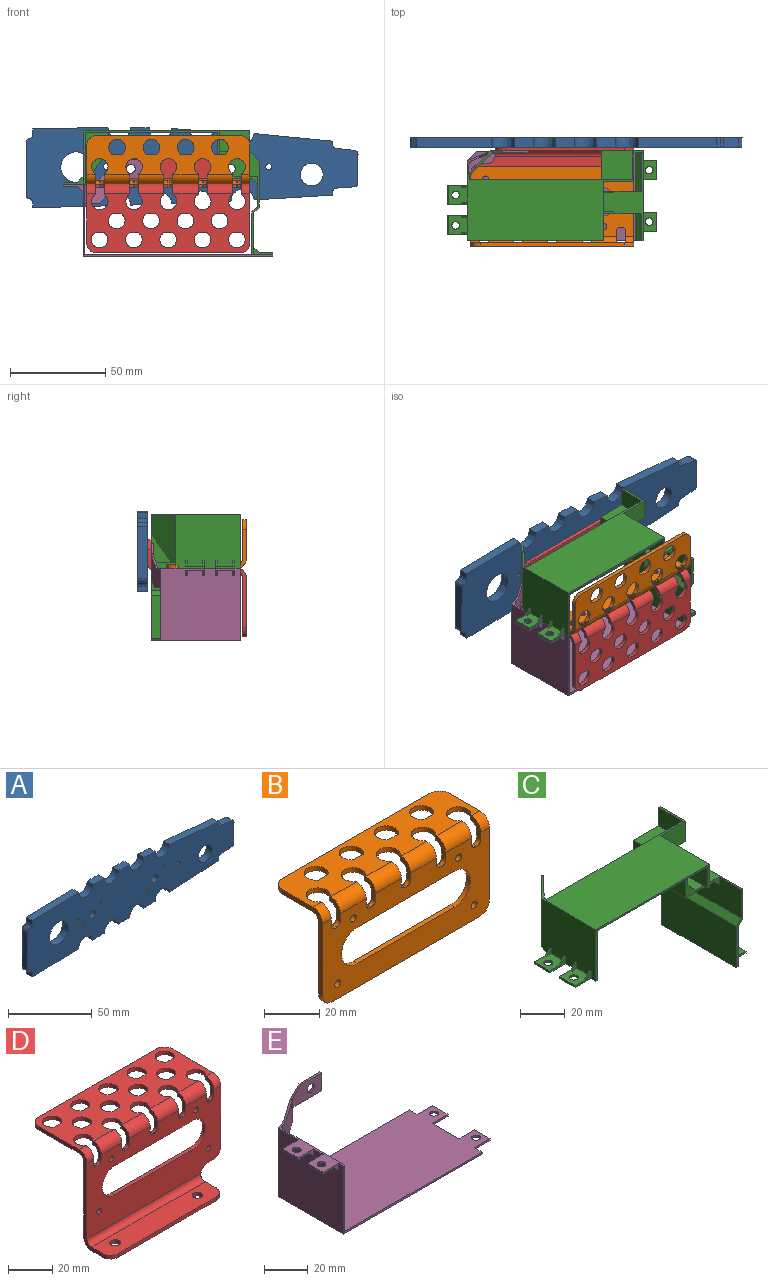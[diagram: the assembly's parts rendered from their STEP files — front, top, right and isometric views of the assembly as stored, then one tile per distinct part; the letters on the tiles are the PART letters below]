
ASSEMBLY  parts=5 mates=7
PART A: 65 faces, bbox 174.9x5.8x42.9 mm
  f0: plane 5x0.18mm, normal (1,0,-0.01), area 0.9mm2, adj f5,f6,f61,f62
  f1: plane 5x0.04mm, normal (1,0,0), area 0.2mm2, adj f7,f8,f61,f62
  f2: plane 5x0.19mm, normal (1,0,0.01), area 0.9mm2, adj f16,f17,f61,f62
  f3: plane 5x0.23mm, normal (1,0,0.02), area 1.1mm2, adj f18,f19,f61,f62
  f4: extruded ~5x0.27mm, area 1.3mm2, adj f20,f21,f61,f62
  f5: extruded ~12.02x6mm, area 93.3mm2, adj f0,f42,f61,f62
  f6: cylinder r=940.53mm len=9.52mm, axis (0,-1,0), area 47.6mm2, adj f0,f7,f61,f62
  f7: extruded ~12.02x6mm, area 94mm2, adj f1,f6,f61,f62
  f8: extruded ~39.35x5mm, area 196.8mm2, adj f1,f9,f61,f62
  f9: plane 5x3.1mm, normal (-1,0,0), area 15.5mm2, adj f8,f10,f61,f62
  f10: extruded ~5x1.99mm, area 14.8mm2, adj f9,f11,f61,f62
  f11: cylinder r=2mm len=5mm, axis (0,-1,0), area 14.7mm2, adj f10,f12,f61,f62
  f12: plane 27.58x5mm, normal (-1,0,0), area 137.9mm2, adj f11,f13,f61,f62
  f13: cylinder r=2mm len=5mm, axis (0,1,0), area 14.7mm2, adj f12,f14,f61,f62
  f14: cylinder r=2mm len=5mm, axis (0,-1,0), area 14.8mm2, adj f13,f15,f61,f62
  f15: plane 5x2.6mm, normal (-1,0,0), area 13mm2, adj f14,f16,f61,f62
  f16: cylinder r=2986.1mm len=39.35mm, axis (0,-1,0), area 196.8mm2, adj f2,f15,f61,f62
  f17: extruded ~12.02x6mm, area 93.4mm2, adj f2,f18,f61,f62
  f18: cylinder r=3206.8mm len=9.52mm, axis (0,-1,0), area 47.7mm2, adj f3,f17,f61,f62
  f19: extruded ~12.02x6mm, area 93.1mm2, adj f3,f20,f61,f62
  f20: cylinder r=3333.11mm len=9.53mm, axis (0,-1,0), area 47.7mm2, adj f4,f19,f61,f62
  f21: extruded ~12.01x6mm, area 92.9mm2, adj f4,f22,f61,f62
  f22: cylinder r=3235.66mm len=9.53mm, axis (0,-1,0), area 47.7mm2, adj f21,f23,f61,f62
  f23: cylinder r=5.99mm len=5mm, axis (0,-1,0), area 1.5mm2, adj f22,f24,f61,f62
  f24: extruded ~12.01x6mm, area 92.7mm2, adj f23,f25,f61,f62
  f25: cylinder r=2917.73mm len=41.28mm, axis (0,-1,0), area 206.8mm2, adj f24,f26,f61,f62
  f26: plane 5x1.64mm, normal (1,0,0), area 8.2mm2, adj f25,f27,f61,f62
  f27: cylinder r=2mm len=5mm, axis (0,-1,0), area 15mm2, adj f26,f28,f61,f62
  f28: cylinder r=2837.04mm len=9.53mm, axis (0,-1,0), area 47.8mm2, adj f27,f29,f61,f62
  f29: cylinder r=2mm len=5mm, axis (0,-1,0), area 15mm2, adj f28,f30,f61,f62
  f30: plane 15.11x5mm, normal (1,0,0), area 75.5mm2, adj f29,f31,f61,f62
  f31: cylinder r=2mm len=5mm, axis (0,1,0), area 14.5mm2, adj f30,f32,f61,f62
  f32: extruded ~7.89x5mm, area 39.7mm2, adj f31,f33,f61,f62
  f33: plane 5x1.83mm, normal (0.11,0,0.99), area 9.2mm2, adj f32,f34,f61,f62
  f34: cylinder r=2mm len=5mm, axis (0,1,0), area 14.6mm2, adj f33,f35,f61,f62
  f35: plane 5x1.73mm, normal (1,0,0), area 8.7mm2, adj f34,f36,f61,f62
  f36: extruded ~41.29x5mm, area 207.4mm2, adj f35,f37,f61,f62
  f37: extruded ~12x6mm, area 92mm2, adj f36,f38,f61,f62
  f38: cylinder r=5.99mm len=5mm, axis (0,1,0), area 2.1mm2, adj f37,f39,f61,f62
  f39: cylinder r=1085.79mm len=9.54mm, axis (0,-1,0), area 47.8mm2, adj f38,f40,f61,f62
  f40: extruded ~12.01x6mm, area 92.6mm2, adj f39,f41,f61,f62
  f41: cylinder r=5.99mm len=5mm, axis (0,1,0), area 1.5mm2, adj f40,f42,f61,f62
  f42: cylinder r=1001.33mm len=9.53mm, axis (0,-1,0), area 47.7mm2, adj f5,f41,f61,f62
  f43: cylinder r=1mm len=5mm, axis (0,-1,0), area 15.7mm2, adj f44,f61,f62
  f44: cylinder r=1mm len=5mm, axis (0,-1,0), area 15.7mm2, adj f43,f61,f62
  f45: cylinder r=1mm len=5mm, axis (0,-1,0), area 15.7mm2, adj f46,f61,f62
  f46: cylinder r=1mm len=5mm, axis (0,-1,0), area 15.7mm2, adj f45,f61,f62
  f47: cylinder r=1mm len=5mm, axis (0,-1,0), area 15.7mm2, adj f48,f61,f62
  f48: cylinder r=1mm len=5mm, axis (0,-1,0), area 15.7mm2, adj f47,f61,f62
  f49: cylinder r=1mm len=5mm, axis (0,-1,0), area 15.7mm2, adj f50,f61,f62
  f50: cylinder r=1mm len=5mm, axis (0,-1,0), area 15.7mm2, adj f49,f61,f62
  f51: cylinder r=2.75mm len=5.16mm, axis (0,1,0), area 43.2mm2, adj f52,f61,f62
  f52: cylinder r=2.75mm len=5.16mm, axis (0,1,0), area 43.2mm2, adj f51,f61,f62
  f53: cylinder r=2.75mm len=5.16mm, axis (0,1,0), area 43.2mm2, adj f54,f61,f62
  f54: cylinder r=2.75mm len=5.16mm, axis (0,1,0), area 43.2mm2, adj f53,f61,f62
  f55: cylinder r=1.55mm len=5mm, axis (0,1,0), area 24.3mm2, adj f56,f61,f62
  f56: cylinder r=1.55mm len=5mm, axis (0,1,0), area 24.3mm2, adj f55,f61,f62
  f57: cylinder r=6mm len=11.27mm, axis (0,1,0), area 94.2mm2, adj f58,f61,f62
  f58: cylinder r=6mm len=11.27mm, axis (0,1,0), area 94.2mm2, adj f57,f61,f62
  f59: extruded ~16.06x8mm, area 125.9mm2, adj f60,f61,f62
  f60: extruded ~16.06x8mm, area 125.9mm2, adj f59,f61,f62
  f61: plane 174.9x42.87mm, normal (0,-1,0), area 5425.6mm2, adj f0,f1,f2,f3,f4,f5,f6,f7
  f62: plane 174.9x42.87mm, normal (0,1,0), area 5425.7mm2, adj f0,f1,f2,f3,f4,f5,f6,f7
  f63: cylinder r=1.55mm len=5mm, axis (0,1,0), area 24.3mm2, adj f61,f62,f64
  f64: cylinder r=1.55mm len=5mm, axis (0,1,0), area 24.3mm2, adj f61,f62,f63
PART B: 84 faces, bbox 85.5x25.5x42 mm
  f0: cylinder r=4.35mm len=8.7mm, axis (0,0,1), area 27.3mm2, adj f15,f16,f25,f27
  f1: cylinder r=4.35mm len=8.7mm, axis (0,0,1), area 27.3mm2, adj f17,f18,f25,f27
  f2: cylinder r=4.35mm len=8.7mm, axis (0,0,1), area 27.3mm2, adj f19,f20,f25,f27
  f3: cylinder r=4.35mm len=8.7mm, axis (0,0,1), area 27.3mm2, adj f21,f22,f25,f27
  f4: plane 75.54x2mm, normal (0,1,0), area 151.1mm2, adj f23,f24,f25,f27
  f5: cylinder r=4.35mm len=8.7mm, axis (0,0,1), area 27.3mm2, adj f14,f25,f26,f27
  f6: plane 4.73x2mm, normal (0,1,0), area 9.5mm2, adj f7,f25,f27
  f7: cylinder r=4.35mm len=8.7mm, axis (0,0,1), area 44.7mm2, adj f6,f25,f27
  f8: plane 4.73x2mm, normal (0,1,0), area 9.5mm2, adj f9,f25,f27
  f9: cylinder r=4.35mm len=8.7mm, axis (0,0,1), area 44.7mm2, adj f8,f25,f27
  f10: plane 4.73x2mm, normal (0,1,0), area 9.5mm2, adj f11,f25,f27
  f11: cylinder r=4.35mm len=8.7mm, axis (0,0,1), area 44.7mm2, adj f10,f25,f27
  f12: cylinder r=4.35mm len=8.7mm, axis (0,0,1), area 44.7mm2, adj f13,f25,f27
  f13: plane 4.73x2mm, normal (0,1,0), area 9.5mm2, adj f12,f25,f27
  f14: cylinder r=4.35mm len=3.65mm, axis (0,0,1), area 8.7mm2, adj f5,f25,f27,f34
  f15: cylinder r=4.35mm len=3.65mm, axis (0,0,1), area 8.7mm2, adj f0,f25,f27,f36
  f16: cylinder r=4.35mm len=3.65mm, axis (0,0,1), area 8.7mm2, adj f0,f25,f27,f40
  f17: cylinder r=4.35mm len=3.65mm, axis (0,0,1), area 8.7mm2, adj f1,f25,f27,f42
  f18: cylinder r=4.35mm len=3.65mm, axis (0,0,1), area 8.7mm2, adj f1,f25,f27,f46
  f19: cylinder r=4.35mm len=3.65mm, axis (0,0,1), area 8.7mm2, adj f2,f25,f27,f48
  f20: cylinder r=4.35mm len=3.65mm, axis (0,0,1), area 8.7mm2, adj f2,f25,f27,f52
  f21: cylinder r=4.35mm len=3.65mm, axis (0,0,1), area 8.7mm2, adj f3,f25,f27,f54
  f22: cylinder r=4.35mm len=3.65mm, axis (0,0,1), area 8.7mm2, adj f3,f25,f27,f58
  f23: cylinder r=5mm len=5mm, axis (0,0,1), area 15.7mm2, adj f4,f25,f27,f60
  f24: cylinder r=5mm len=5mm, axis (0,0,1), area 15.7mm2, adj f4,f25,f27,f64
  f25: plane 85.54x20.45mm, normal (0,0,-1), area 1214.1mm2, adj f0,f1,f2,f3,f4,f5,f6,f7
  f26: cylinder r=4.35mm len=3.65mm, axis (0,0,1), area 8.7mm2, adj f5,f25,f27,f66
  f27: plane 85.54x20.45mm, normal (0,0,1), area 1214.1mm2, adj f0,f1,f2,f3,f4,f5,f6,f7
  f28: cylinder r=5mm len=5mm, axis (1,0,0), area 34.6mm2, adj f27,f64,f66,f80
  f29: cylinder r=5mm len=5mm, axis (-1,0,0), area 34.6mm2, adj f27,f58,f60,f80
  f30: cylinder r=5mm len=13.27mm, axis (-1,0,0), area 104.2mm2, adj f27,f52,f54,f80
  f31: cylinder r=5mm len=13.27mm, axis (-1,0,0), area 104.2mm2, adj f27,f46,f48,f80
  f32: cylinder r=5mm len=13.27mm, axis (-1,0,0), area 104.2mm2, adj f27,f40,f42,f80
  f33: cylinder r=5mm len=13.27mm, axis (-1,0,0), area 104.2mm2, adj f27,f34,f36,f80
  f34: plane 8x5.41mm, normal (1,0,0), area 19.4mm2, adj f14,f25,f27,f33,f35,f69,f80,f82
  f35: cylinder r=3mm len=13.27mm, axis (1,0,0), area 62.5mm2, adj f25,f34,f36,f82
  f36: plane 8x5.41mm, normal (-1,0,0), area 19.4mm2, adj f15,f25,f27,f33,f35,f37,f80,f82
  f37: cylinder r=2mm len=2mm, axis (0,1,0), area 6.3mm2, adj f36,f38,f80,f82
  f38: plane 2x0.73mm, normal (0,0,1), area 1.5mm2, adj f37,f39,f80,f82
  f39: cylinder r=2mm len=2mm, axis (0,1,0), area 6.3mm2, adj f38,f40,f80,f82
  f40: plane 8x5.41mm, normal (1,0,0), area 19.4mm2, adj f16,f25,f27,f32,f39,f41,f80,f82
  f41: cylinder r=3mm len=13.27mm, axis (-1,0,0), area 62.5mm2, adj f25,f40,f42,f82
  f42: plane 8x5.41mm, normal (-1,0,0), area 19.4mm2, adj f17,f25,f27,f32,f41,f43,f80,f82
  f43: cylinder r=2mm len=2mm, axis (0,1,0), area 6.3mm2, adj f42,f44,f80,f82
  f44: plane 2x0.73mm, normal (0,0,1), area 1.5mm2, adj f43,f45,f80,f82
  f45: cylinder r=2mm len=2mm, axis (0,1,0), area 6.3mm2, adj f44,f46,f80,f82
  f46: plane 8x5.41mm, normal (1,0,0), area 19.4mm2, adj f18,f25,f27,f31,f45,f47,f80,f82
  f47: cylinder r=3mm len=13.27mm, axis (-1,0,0), area 62.5mm2, adj f25,f46,f48,f82
  f48: plane 8x5.41mm, normal (-1,0,0), area 19.4mm2, adj f19,f25,f27,f31,f47,f49,f80,f82
  f49: cylinder r=2mm len=2mm, axis (0,1,0), area 6.3mm2, adj f48,f50,f80,f82
  f50: plane 2x0.73mm, normal (0,0,1), area 1.5mm2, adj f49,f51,f80,f82
  f51: cylinder r=2mm len=2mm, axis (0,1,0), area 6.3mm2, adj f50,f52,f80,f82
  f52: plane 8x5.41mm, normal (1,0,0), area 19.4mm2, adj f20,f25,f27,f30,f51,f53,f80,f82
  f53: cylinder r=3mm len=13.27mm, axis (-1,0,0), area 62.5mm2, adj f25,f52,f54,f82
  f54: plane 8x5.41mm, normal (-1,0,0), area 19.4mm2, adj f21,f25,f27,f30,f53,f55,f80,f82
  f55: cylinder r=2mm len=2mm, axis (0,1,0), area 6.3mm2, adj f54,f56,f80,f82
  f56: plane 2x0.73mm, normal (0,0,1), area 1.5mm2, adj f55,f57,f80,f82
  f57: cylinder r=2mm len=2mm, axis (0,1,0), area 6.3mm2, adj f56,f58,f80,f82
  f58: plane 8x5.41mm, normal (1,0,0), area 19.4mm2, adj f22,f25,f27,f29,f57,f59,f80,f82
  f59: cylinder r=3mm len=4.4mm, axis (-1,0,0), area 20.7mm2, adj f25,f58,f60,f82
  f60: plane 37x20.45mm, normal (-1,0,0), area 107.5mm2, adj f23,f25,f27,f29,f59,f61,f80,f82
  f61: cylinder r=5mm len=5mm, axis (0,-1,0), area 15.7mm2, adj f60,f62,f80,f82
  f62: plane 75.54x2mm, normal (0,0,-1), area 151.1mm2, adj f61,f63,f80,f82
  f63: cylinder r=5mm len=5mm, axis (0,1,0), area 15.7mm2, adj f62,f64,f80,f82
  f64: plane 37x20.45mm, normal (1,0,0), area 107.5mm2, adj f24,f25,f27,f28,f63,f65,f80,f82
  f65: cylinder r=3mm len=4.4mm, axis (1,0,0), area 20.7mm2, adj f25,f64,f66,f82
  f66: plane 8x5.41mm, normal (-1,0,0), area 19.4mm2, adj f25,f26,f27,f28,f65,f67,f80,f82
  f67: cylinder r=2mm len=2mm, axis (0,1,0), area 6.3mm2, adj f66,f68,f80,f82
  f68: plane 2x0.73mm, normal (0,0,1), area 1.5mm2, adj f67,f69,f80,f82
  f69: cylinder r=2mm len=2mm, axis (0,1,0), area 6.3mm2, adj f34,f68,f80,f82
  f70: plane 50x2mm, normal (0,0,1), area 100mm2, adj f71,f73,f80,f82
  f71: cylinder r=8mm len=16mm, axis (0,1,0), area 50.3mm2, adj f70,f72,f80,f82
  f72: plane 50x2mm, normal (0,0,-1), area 100mm2, adj f71,f73,f80,f82
  f73: cylinder r=8mm len=16mm, axis (0,1,0), area 50.3mm2, adj f70,f72,f80,f82
  f74: cylinder r=1.5mm len=3mm, axis (0,1,0), area 9.4mm2, adj f75,f80,f82
  f75: cylinder r=1.5mm len=3mm, axis (0,1,0), area 9.4mm2, adj f74,f80,f82
  f76: cylinder r=1.5mm len=3mm, axis (0,1,0), area 9.4mm2, adj f77,f80,f82
  f77: cylinder r=1.5mm len=3mm, axis (0,1,0), area 9.4mm2, adj f76,f80,f82
  f78: cylinder r=1.5mm len=3mm, axis (0,1,0), area 9.4mm2, adj f79,f80,f82
  f79: cylinder r=1.5mm len=3mm, axis (0,1,0), area 9.4mm2, adj f78,f80,f82
  f80: plane 85.54x37mm, normal (0,-1,0), area 2015mm2, adj f28,f29,f30,f31,f32,f33,f34,f36
  f81: cylinder r=1.5mm len=3mm, axis (0,1,0), area 9.4mm2, adj f80,f82,f83
  f82: plane 85.54x37mm, normal (0,1,0), area 2015mm2, adj f34,f35,f36,f37,f38,f39,f40,f41
  f83: cylinder r=1.5mm len=3mm, axis (0,1,0), area 9.4mm2, adj f80,f81,f82
PART C: 83 faces, bbox 109.5x47x65 mm
  f0: plane 3x3mm, normal (-0.71,0,0.71), area 4.2mm2, adj f4,f72,f74,f78
  f1: plane 3x3mm, normal (-0.71,0,0.71), area 4.2mm2, adj f4,f73,f74,f79
  f2: plane 3x3mm, normal (-0.71,0,0.71), area 4.2mm2, adj f4,f68,f70,f76
  f3: plane 3x3mm, normal (-0.71,0,0.71), area 4.2mm2, adj f4,f69,f70,f77
  f4: plane 34x28mm, normal (-1,0,0), area 918.1mm2, adj f0,f1,f2,f3,f17,f18,f30,f66
  f5: plane 2.57x1.84mm, normal (0,0,-1), area 2.1mm2, adj f16,f30,f31,f33,f67
  f6: plane 47x15.59mm, normal (-1,0,0), area 710.5mm2, adj f10,f11,f12,f13,f23,f24,f39,f40
  f7: plane 3x3mm, normal (0.71,0,0.71), area 4.2mm2, adj f9,f53,f54,f63
  f8: plane 3x3mm, normal (0.71,0,0.71), area 4.2mm2, adj f9,f48,f50,f59
  f9: plane 47x22mm, normal (1,0,0), area 1002mm2, adj f7,f8,f24,f39,f44,f47,f48,f49
  f10: plane 33x21mm, normal (0,0,-1), area 284mm2, adj f6,f11,f12,f14,f15,f23,f24,f40
  f11: plane 21x15.5mm, normal (0,-1,0), area 52.1mm2, adj f6,f10,f13,f14,f15,f29,f35,f40
  f12: plane 20x9.5mm, normal (0,1,0), area 39.6mm2, adj f6,f10,f13,f14,f37,f42
  f13: plane 46x21mm, normal (0,0,1), area 275mm2, adj f6,f11,f12,f14,f23,f34,f35,f36
  f14: plane 46x25mm, normal (1,0,0), area 787mm2, adj f10,f11,f12,f13,f18,f23,f25,f28
  f15: plane 47x24mm, normal (-1,0,0), area 818mm2, adj f10,f11,f19,f20,f24,f27,f29,f82
  f16: plane 35x28mm, normal (1,0,0), area 908.5mm2, adj f5,f17,f18,f19,f20,f31,f66,f67
  f17: plane 27.01x1.01mm, normal (0,-1,0), area 27mm2, adj f4,f16,f66,f82
  f18: plane 87.5x47mm, normal (0,0,1), area 2338.8mm2, adj f4,f14,f16,f19,f22,f24,f26,f28
  f19: plane 85.5x10mm, normal (0,1,0), area 229.5mm2, adj f15,f16,f18,f20,f26,f27
  f20: plane 69.5x32mm, normal (0,0,-1), area 2224.2mm2, adj f15,f16,f19,f82
  f21: cylinder r=2.35mm len=4.7mm, axis (0,1,0), area 14.8mm2, adj f23,f24
  f22: plane 16x11mm, normal (1,0,0), area 176mm2, adj f18,f24,f25,f28,f64
  f23: plane 21x17mm, normal (0,-1,0), area 267.7mm2, adj f6,f10,f13,f14,f21,f25,f34,f64
  f24: plane 65x22mm, normal (0,1,0), area 350.9mm2, adj f6,f9,f10,f15,f18,f21,f22,f26
  f25: plane 16x15mm, normal (0,0,-1), area 240mm2, adj f14,f22,f23,f28
  f26: plane 15x10mm, normal (-1,0,0), area 150mm2, adj f18,f19,f24,f27
  f27: plane 16x15mm, normal (0,0,1), area 240mm2, adj f15,f19,f24,f26
  f28: plane 16x11mm, normal (0,-1,0), area 176mm2, adj f14,f18,f22,f25
  f29: plane 14x1mm, normal (0,0,-1), area 14mm2, adj f11,f14,f15,f82
  f30: plane 26x13mm, normal (-0.72,0.69,0), area 338.2mm2, adj f4,f5,f18,f32,f33,f67
  f31: plane 25x12.71mm, normal (0.72,-0.69,0), area 327.5mm2, adj f5,f16,f18,f32,f33
  f32: plane 10x0.72mm, normal (0.69,0.72,0), area 10mm2, adj f18,f30,f31,f33
  f33: plane 15x11.53mm, normal (0.49,0.51,-0.71), area 21.2mm2, adj f5,f30,f31,f32
  f34: plane 47x24mm, normal (1,0,0), area 760mm2, adj f13,f23,f24,f39,f44,f64
  f35: plane 5.5x5.5mm, normal (0.71,0,0.71), area 7.8mm2, adj f11,f13,f14,f36
  f36: plane 5.5x5.5mm, normal (0,1,0), area 15.1mm2, adj f13,f14,f35
  f37: plane 5.5x5.5mm, normal (0.71,0,0.71), area 7.8mm2, adj f12,f13,f14,f38
  f38: plane 5.5x5.5mm, normal (0,-1,0), area 15.1mm2, adj f13,f14,f37
  f39: plane 41x4mm, normal (0,-1,0), area 42.2mm2, adj f6,f9,f13,f34,f44,f45,f46,f47
  f40: plane 3x3mm, normal (-0.71,0,-0.71), area 4.2mm2, adj f6,f10,f11,f41
  f41: plane 3x3mm, normal (0,1,0), area 4.5mm2, adj f6,f10,f40
  f42: plane 3x3mm, normal (-0.71,0,-0.71), area 4.2mm2, adj f6,f10,f12,f43
  f43: plane 3x3mm, normal (0,-1,0), area 4.5mm2, adj f6,f10,f42
  f44: plane 47x3mm, normal (0.71,0,-0.71), area 199.4mm2, adj f9,f24,f34,f39
  f45: plane 47x3mm, normal (-0.71,0,0.71), area 199.4mm2, adj f6,f24,f39,f46
  f46: plane 47x22.41mm, normal (-1,0,0), area 1053.5mm2, adj f24,f39,f45,f47
  f47: plane 47x11mm, normal (0,0,-1), area 221.9mm2, adj f9,f24,f39,f46,f48,f49,f51,f52
  f48: plane 10x4mm, normal (0,-1,0), area 14.5mm2, adj f8,f9,f47,f50,f51
  f49: plane 10x4mm, normal (0,1,0), area 14.5mm2, adj f9,f47,f50,f51,f58
  f50: plane 10x10mm, normal (0,0,1), area 81.4mm2, adj f8,f9,f48,f49,f51,f57,f58,f59
  f51: plane 10x1mm, normal (1,0,0), area 10mm2, adj f47,f48,f49,f50
  f52: plane 10x4mm, normal (0,1,0), area 14.5mm2, adj f9,f47,f53,f55,f61
  f53: plane 10x10mm, normal (0,0,1), area 81.4mm2, adj f7,f9,f52,f54,f55,f56,f61,f62
  f54: plane 10x4mm, normal (0,-1,0), area 14.5mm2, adj f7,f9,f47,f53,f55
  f55: plane 10x1mm, normal (1,0,0), area 10mm2, adj f47,f52,f53,f54
  f56: cylinder r=2mm len=4mm, axis (0,0,1), area 12.6mm2, adj f47,f53
  f57: cylinder r=2mm len=4mm, axis (0,0,1), area 12.6mm2, adj f47,f50
  f58: plane 3x3mm, normal (0.71,0,0.71), area 4.2mm2, adj f9,f49,f50,f60
  f59: plane 3x3mm, normal (0,1,0), area 4.5mm2, adj f8,f9,f50
  f60: plane 3x3mm, normal (0,-1,0), area 4.5mm2, adj f9,f50,f58
  f61: plane 3x3mm, normal (0.71,0,0.71), area 4.2mm2, adj f9,f52,f53,f62
  f62: plane 3x3mm, normal (0,-1,0), area 4.5mm2, adj f9,f53,f61
  f63: plane 3x3mm, normal (0,1,0), area 4.5mm2, adj f7,f9,f53
  f64: plane 5x5mm, normal (0.71,0,0.71), area 7.1mm2, adj f22,f23,f24,f34
  f65: plane 3x3mm, normal (-0.71,0,-0.71), area 4.2mm2, adj f6,f10,f23,f24
  f66: plane 32x11mm, normal (0,0,-1), area 206.9mm2, adj f4,f16,f17,f67,f68,f69,f71,f72
  f67: plane 3x3mm, normal (0,0.71,-0.71), area 3.6mm2, adj f4,f5,f16,f30,f66
  f68: plane 10x4mm, normal (0,1,0), area 14.5mm2, adj f2,f4,f66,f70,f71
  f69: plane 10x4mm, normal (0,-1,0), area 14.5mm2, adj f3,f4,f66,f70,f71
  f70: plane 10x10mm, normal (0,0,1), area 81.4mm2, adj f2,f3,f4,f68,f69,f71,f76,f77
  f71: plane 10x1mm, normal (-1,0,0), area 10mm2, adj f66,f68,f69,f70
  f72: plane 10x4mm, normal (0,1,0), area 14.5mm2, adj f0,f4,f66,f74,f75
  f73: plane 10x4mm, normal (0,-1,0), area 14.5mm2, adj f1,f4,f66,f74,f75
  f74: plane 10x10mm, normal (0,0,1), area 81.4mm2, adj f0,f1,f4,f72,f73,f75,f78,f79
  f75: plane 10x1mm, normal (-1,0,0), area 10mm2, adj f66,f72,f73,f74
  f76: plane 3x3mm, normal (0,-1,0), area 4.5mm2, adj f2,f4,f70
  f77: plane 3x3mm, normal (0,1,0), area 4.5mm2, adj f3,f4,f70
  f78: plane 3x3mm, normal (0,-1,0), area 4.5mm2, adj f0,f4,f74
  f79: plane 3x3mm, normal (0,1,0), area 4.5mm2, adj f1,f4,f74
  f80: cylinder r=2mm len=4mm, axis (0,0,1), area 12.6mm2, adj f66,f74
  f81: cylinder r=2mm len=4mm, axis (0,0,1), area 12.6mm2, adj f66,f70
  f82: plane 71.51x12.51mm, normal (0,-1,0), area 83mm2, adj f4,f14,f15,f17,f18,f20,f29
PART D: 106 faces, bbox 85.5x51x52 mm
  f0: plane 75.54x2mm, normal (0,1,0), area 151.1mm2, adj f30,f43,f44,f45
  f1: cylinder r=4.35mm len=8.7mm, axis (0,0,1), area 27.3mm2, adj f31,f32,f43,f45
  f2: cylinder r=4.35mm len=8.7mm, axis (0,0,1), area 27.3mm2, adj f33,f34,f43,f45
  f3: cylinder r=4.35mm len=8.7mm, axis (0,0,1), area 27.3mm2, adj f35,f36,f43,f45
  f4: cylinder r=4.35mm len=8.7mm, axis (0,0,1), area 27.3mm2, adj f37,f38,f43,f45
  f5: cylinder r=4.35mm len=8.7mm, axis (0,0,1), area 27.3mm2, adj f39,f40,f43,f45
  f6: plane 4.73x2mm, normal (0,1,0), area 9.5mm2, adj f7,f43,f45
  f7: cylinder r=4.35mm len=8.7mm, axis (0,0,1), area 44.7mm2, adj f6,f43,f45
  f8: plane 4.73x2mm, normal (0,1,0), area 9.5mm2, adj f9,f43,f45
  f9: cylinder r=4.35mm len=8.7mm, axis (0,0,1), area 44.7mm2, adj f8,f43,f45
  f10: plane 4.73x2mm, normal (0,1,0), area 9.5mm2, adj f11,f43,f45
  f11: cylinder r=4.35mm len=8.7mm, axis (0,0,1), area 44.7mm2, adj f10,f43,f45
  f12: plane 4.73x2mm, normal (0,1,0), area 9.5mm2, adj f13,f43,f45
  f13: cylinder r=4.35mm len=8.7mm, axis (0,0,1), area 44.7mm2, adj f12,f43,f45
  f14: plane 4.73x2mm, normal (0,1,0), area 9.5mm2, adj f15,f43,f45
  f15: cylinder r=4.35mm len=8.7mm, axis (0,0,1), area 44.7mm2, adj f14,f43,f45
  f16: plane 4.73x2mm, normal (0,1,0), area 9.5mm2, adj f17,f43,f45
  f17: cylinder r=4.35mm len=8.7mm, axis (0,0,1), area 44.7mm2, adj f16,f43,f45
  f18: cylinder r=4.35mm len=8.7mm, axis (0,0,1), area 44.7mm2, adj f19,f43,f45
  f19: plane 4.73x2mm, normal (0,1,0), area 9.5mm2, adj f18,f43,f45
  f20: plane 4.73x2mm, normal (0,1,0), area 9.5mm2, adj f21,f43,f45
  f21: cylinder r=4.35mm len=8.7mm, axis (0,0,1), area 44.7mm2, adj f20,f43,f45
  f22: cylinder r=4.35mm len=8.7mm, axis (0,0,1), area 44.7mm2, adj f23,f43,f45
  f23: plane 4.73x2mm, normal (0,1,0), area 9.5mm2, adj f22,f43,f45
  f24: plane 62.54x2mm, normal (0,-1,0), area 125.1mm2, adj f29,f41,f42,f46
  f25: cylinder r=2.39mm len=4.48mm, axis (0,0,-1), area 15mm2, adj f26,f41,f46
  f26: cylinder r=2.39mm len=4.48mm, axis (0,0,-1), area 15mm2, adj f25,f41,f46
  f27: cylinder r=2.39mm len=4.48mm, axis (0,0,-1), area 15mm2, adj f28,f41,f46
  f28: cylinder r=2.39mm len=4.48mm, axis (0,0,-1), area 15mm2, adj f27,f41,f46
  f29: cylinder r=5mm len=5mm, axis (0,0,1), area 15.7mm2, adj f24,f41,f46,f47
  f30: cylinder r=5mm len=5mm, axis (0,0,1), area 15.7mm2, adj f0,f43,f45,f56
  f31: cylinder r=4.35mm len=3.65mm, axis (0,0,1), area 8.7mm2, adj f1,f43,f45,f58
  f32: cylinder r=4.35mm len=3.65mm, axis (0,0,1), area 8.7mm2, adj f1,f43,f45,f62
  f33: cylinder r=4.35mm len=3.65mm, axis (0,0,1), area 8.7mm2, adj f2,f43,f45,f64
  f34: cylinder r=4.35mm len=3.65mm, axis (0,0,1), area 8.7mm2, adj f2,f43,f45,f68
  f35: cylinder r=4.35mm len=3.65mm, axis (0,0,1), area 8.7mm2, adj f3,f43,f45,f70
  f36: cylinder r=4.35mm len=3.65mm, axis (0,0,1), area 8.7mm2, adj f3,f43,f45,f74
  f37: cylinder r=4.35mm len=3.65mm, axis (0,0,1), area 8.7mm2, adj f4,f43,f45,f76
  f38: cylinder r=4.35mm len=3.65mm, axis (0,0,1), area 8.7mm2, adj f4,f43,f45,f80
  f39: cylinder r=4.35mm len=3.65mm, axis (0,0,1), area 8.7mm2, adj f5,f43,f45,f82
  f40: cylinder r=4.35mm len=3.65mm, axis (0,0,1), area 8.7mm2, adj f5,f43,f45,f86
  f41: plane 72.54x12mm, normal (0,0,1), area 823.9mm2, adj f24,f25,f26,f27,f28,f29,f42,f47
  f42: cylinder r=5mm len=5mm, axis (0,0,1), area 15.7mm2, adj f24,f41,f46,f88
  f43: plane 85.54x31mm, normal (0,0,-1), area 1830.3mm2, adj f0,f1,f2,f3,f4,f5,f6,f7
  f44: cylinder r=5mm len=5mm, axis (0,0,1), area 15.7mm2, adj f0,f43,f45,f88
  f45: plane 85.54x31mm, normal (0,0,1), area 1830.3mm2, adj f0,f1,f2,f3,f4,f5,f6,f7
  f46: plane 72.54x12mm, normal (0,0,-1), area 823.9mm2, adj f24,f25,f26,f27,f28,f29,f42,f47
  f47: plane 11.83x3.69mm, normal (1,0,0), area 23.9mm2, adj f29,f41,f46,f53,f89,f90
  f48: cylinder r=5mm len=13.27mm, axis (-1,0,0), area 104.2mm2, adj f45,f80,f82,f102
  f49: cylinder r=5mm len=13.27mm, axis (-1,0,0), area 104.2mm2, adj f45,f74,f76,f102
  f50: cylinder r=5mm len=13.27mm, axis (-1,0,0), area 104.2mm2, adj f45,f68,f70,f102
  f51: cylinder r=5mm len=13.27mm, axis (-1,0,0), area 104.2mm2, adj f45,f62,f64,f102
  f52: cylinder r=5mm len=5mm, axis (1,0,0), area 34.6mm2, adj f45,f56,f58,f102
  f53: cylinder r=3mm len=72.71mm, axis (-1,0,0), area 341.9mm2, adj f41,f47,f88,f90,f102
  f54: cylinder r=5mm len=5mm, axis (-1,0,0), area 34.6mm2, adj f45,f86,f88,f102
  f55: cylinder r=5mm len=5mm, axis (0,1,0), area 15.7mm2, adj f56,f91,f102,f104
  f56: plane 38.31x31mm, normal (1,0,0), area 131.2mm2, adj f30,f43,f45,f52,f55,f57,f102,f104
  f57: cylinder r=3mm len=4.4mm, axis (-1,0,0), area 20.7mm2, adj f43,f56,f58,f104
  f58: plane 8x5.41mm, normal (-1,0,0), area 19.4mm2, adj f31,f43,f45,f52,f57,f59,f102,f104
  f59: cylinder r=2mm len=2mm, axis (0,1,0), area 6.3mm2, adj f58,f60,f102,f104
  f60: plane 2x0.73mm, normal (0,0,1), area 1.5mm2, adj f59,f61,f102,f104
  f61: cylinder r=2mm len=2mm, axis (0,1,0), area 6.3mm2, adj f60,f62,f102,f104
  f62: plane 8x5.41mm, normal (1,0,0), area 19.4mm2, adj f32,f43,f45,f51,f61,f63,f102,f104
  f63: cylinder r=3mm len=13.27mm, axis (-1,0,0), area 62.5mm2, adj f43,f62,f64,f104
  f64: plane 8x5.41mm, normal (-1,0,0), area 19.4mm2, adj f33,f43,f45,f51,f63,f65,f102,f104
  f65: cylinder r=2mm len=2mm, axis (0,1,0), area 6.3mm2, adj f64,f66,f102,f104
  f66: plane 2x0.73mm, normal (0,0,1), area 1.5mm2, adj f65,f67,f102,f104
  f67: cylinder r=2mm len=2mm, axis (0,1,0), area 6.3mm2, adj f66,f68,f102,f104
  f68: plane 8x5.41mm, normal (1,0,0), area 19.4mm2, adj f34,f43,f45,f50,f67,f69,f102,f104
  f69: cylinder r=3mm len=13.27mm, axis (-1,0,0), area 62.5mm2, adj f43,f68,f70,f104
  f70: plane 8x5.41mm, normal (-1,0,0), area 19.4mm2, adj f35,f43,f45,f50,f69,f71,f102,f104
  f71: cylinder r=2mm len=2mm, axis (0,1,0), area 6.3mm2, adj f70,f72,f102,f104
  f72: plane 2x0.73mm, normal (0,0,1), area 1.5mm2, adj f71,f73,f102,f104
  f73: cylinder r=2mm len=2mm, axis (0,1,0), area 6.3mm2, adj f72,f74,f102,f104
  f74: plane 8x5.41mm, normal (1,0,0), area 19.4mm2, adj f36,f43,f45,f49,f73,f75,f102,f104
  f75: cylinder r=3mm len=13.27mm, axis (-1,0,0), area 62.5mm2, adj f43,f74,f76,f104
  f76: plane 8x5.41mm, normal (-1,0,0), area 19.4mm2, adj f37,f43,f45,f49,f75,f77,f102,f104
  f77: cylinder r=2mm len=2mm, axis (0,1,0), area 6.3mm2, adj f76,f78,f102,f104
  f78: plane 2x0.73mm, normal (0,0,1), area 1.5mm2, adj f77,f79,f102,f104
  f79: cylinder r=2mm len=2mm, axis (0,1,0), area 6.3mm2, adj f78,f80,f102,f104
  f80: plane 8x5.41mm, normal (1,0,0), area 19.4mm2, adj f38,f43,f45,f48,f79,f81,f102,f104
  f81: cylinder r=3mm len=13.27mm, axis (-1,0,0), area 62.5mm2, adj f43,f80,f82,f104
  f82: plane 8x5.41mm, normal (-1,0,0), area 19.4mm2, adj f39,f43,f45,f48,f81,f83,f102,f104
  f83: cylinder r=2mm len=2mm, axis (0,1,0), area 6.3mm2, adj f82,f84,f102,f104
  f84: plane 2x0.73mm, normal (0,0,1), area 1.5mm2, adj f83,f85,f102,f104
  f85: cylinder r=2mm len=2mm, axis (0,1,0), area 6.3mm2, adj f84,f86,f102,f104
  f86: plane 8x5.41mm, normal (1,0,0), area 19.4mm2, adj f40,f43,f45,f54,f85,f87,f102,f104
  f87: cylinder r=3mm len=4.4mm, axis (-1,0,0), area 20.7mm2, adj f43,f86,f88,f104
  f88: plane 52x41mm, normal (-1,0,0), area 175.1mm2, adj f41,f42,f43,f44,f45,f46,f53,f54
  f89: cylinder r=5mm len=72.71mm, axis (-1,0,0), area 569.8mm2, adj f46,f47,f88,f90,f104
  f90: cylinder r=5mm len=5mm, axis (0,1,0), area 15.8mm2, adj f47,f53,f89,f91,f102,f104
  f91: plane 3x2mm, normal (0,0,-1), area 6mm2, adj f55,f90,f102,f104
  f92: cylinder r=8mm len=16mm, axis (0,-1,0), area 50.3mm2, adj f93,f95,f102,f104
  f93: plane 50x2mm, normal (0,0,1), area 100mm2, adj f92,f94,f102,f104
  f94: cylinder r=8mm len=16mm, axis (0,-1,0), area 50.3mm2, adj f93,f95,f102,f104
  f95: plane 50x2mm, normal (0,0,-1), area 100mm2, adj f92,f94,f102,f104
  f96: cylinder r=1.5mm len=3mm, axis (0,-1,0), area 9.4mm2, adj f97,f102,f104
  f97: cylinder r=1.5mm len=3mm, axis (0,-1,0), area 9.4mm2, adj f96,f102,f104
  f98: cylinder r=1.5mm len=3mm, axis (0,-1,0), area 9.4mm2, adj f99,f102,f104
  f99: cylinder r=1.5mm len=3mm, axis (0,-1,0), area 9.4mm2, adj f98,f102,f104
  f100: cylinder r=1.5mm len=3mm, axis (0,-1,0), area 9.4mm2, adj f101,f102,f104
  f101: cylinder r=1.5mm len=3mm, axis (0,-1,0), area 9.4mm2, adj f100,f102,f104
  f102: plane 85.54x42mm, normal (0,-1,0), area 2405.3mm2, adj f48,f49,f50,f51,f52,f53,f54,f55
  f103: cylinder r=1.5mm len=3mm, axis (0,-1,0), area 9.4mm2, adj f102,f104,f105
  f104: plane 85.54x42mm, normal (0,1,0), area 2405.3mm2, adj f55,f56,f57,f58,f59,f60,f61,f62
  f105: cylinder r=1.5mm len=3mm, axis (0,-1,0), area 9.4mm2, adj f102,f103,f104
PART E: 55 faces, bbox 109.5x47.6x51 mm
  f0: plane 3x3mm, normal (-0.71,0,-0.71), area 4.2mm2, adj f2,f39,f40,f51
  f1: plane 3x3mm, normal (-0.71,0,-0.71), area 4.2mm2, adj f2,f44,f45,f49
  f2: plane 42x38mm, normal (-1,0,0), area 1564mm2, adj f0,f1,f3,f7,f11,f12,f13,f38
  f3: plane 27x1mm, normal (0,1,0), area 27mm2, adj f2,f8,f10,f15
  f4: plane 17x1mm, normal (1,0,0), area 17mm2, adj f10,f11,f29,f30
  f5: plane 5x1mm, normal (1,0,0), area 5mm2, adj f10,f11,f12,f26
  f6: plane 6.5x0.93mm, normal (0.93,0.36,0), area 6.5mm2, adj f13,f14,f24,f35
  f7: plane 44.31x16.36mm, normal (0,0,1), area 223.4mm2, adj f2,f8,f12,f13,f14,f16,f33,f39
  f8: plane 42x37mm, normal (1,0,0), area 1526.5mm2, adj f3,f7,f10,f12,f15,f33
  f9: plane 10x1mm, normal (0,1,0), area 10mm2, adj f10,f11,f31,f36
  f10: plane 99.5x47mm, normal (0,0,1), area 4326.9mm2, adj f3,f4,f5,f8,f9,f12,f26,f27
  f11: plane 99.5x47mm, normal (0,0,-1), area 4368.9mm2, adj f2,f4,f5,f9,f12,f26,f27,f28
  f12: plane 89.5x38mm, normal (0,-1,0), area 126.5mm2, adj f2,f5,f7,f8,f10,f11
  f13: plane 17.5x13mm, normal (-0.36,0.93,0), area 154.9mm2, adj f2,f6,f7,f15,f16,f18,f24
  f14: plane 16.56x11.84mm, normal (0.36,-0.93,0), area 124.1mm2, adj f6,f7,f15,f16,f22,f24,f25,f33
  f15: plane 8.69x5.95mm, normal (0,0,-1), area 9mm2, adj f3,f8,f13,f14,f24,f33
  f16: plane 7.65x7.58mm, normal (-0.66,-0.25,0.71), area 10.4mm2, adj f7,f13,f14,f20,f21,f25
  f17: plane 13.5x1.07mm, normal (0,0,1), area 14.5mm2, adj f18,f19,f20,f34
  f18: plane 19x11.5mm, normal (0,1,0), area 158mm2, adj f13,f17,f19,f22,f23,f34,f35
  f19: plane 10x1.07mm, normal (1,0,0), area 10.7mm2, adj f17,f18,f20,f22
  f20: plane 19x10mm, normal (0,-1,0), area 155.1mm2, adj f16,f17,f19,f21,f22,f23,f25,f34
  f21: plane 1.07x0.38mm, normal (-1,0,0), area 0.2mm2, adj f16,f20,f34
  f22: plane 19.52x1.27mm, normal (0,0,-1), area 19.1mm2, adj f14,f18,f19,f20,f25,f35
  f23: cylinder r=2.35mm len=4.7mm, axis (0,-1,0), area 15.8mm2, adj f18,f20
  f24: plane 5.03x5mm, normal (0.66,0.25,-0.71), area 7.1mm2, adj f6,f13,f14,f15
  f25: cylinder r=3mm len=4.64mm, axis (0,0,1), area 4.5mm2, adj f14,f16,f20,f22
  f26: plane 10x1mm, normal (0,-1,0), area 10mm2, adj f5,f10,f11,f27
  f27: plane 10x1mm, normal (1,0,0), area 10mm2, adj f10,f11,f26,f29
  f28: cylinder r=2mm len=4mm, axis (0,0,1), area 12.6mm2, adj f10,f11
  f29: plane 10x1mm, normal (0,1,0), area 10mm2, adj f4,f10,f11,f27
  f30: plane 10x1mm, normal (0,-1,0), area 10mm2, adj f4,f10,f11,f31
  f31: plane 10x1mm, normal (1,0,0), area 10mm2, adj f9,f10,f11,f30
  f32: cylinder r=2mm len=4mm, axis (0,0,1), area 12.6mm2, adj f10,f11
  f33: cylinder r=3mm len=10mm, axis (0,0,-1), area 36.1mm2, adj f7,f8,f14,f15
  f34: plane 5.5x5.5mm, normal (-0.71,0,0.71), area 8.3mm2, adj f17,f18,f20,f21
  f35: cylinder r=1.5mm len=1.76mm, axis (0.36,-0.93,0), area 1.9mm2, adj f6,f14,f18,f22
  f36: plane 5x1mm, normal (1,0,0), area 5mm2, adj f9,f10,f11,f37
  f37: plane 84.5x1mm, normal (0,1,0), area 84.5mm2, adj f10,f11,f36,f38
  f38: plane 5x5mm, normal (-0.71,0.71,0), area 7.1mm2, adj f2,f10,f11,f37
  f39: plane 10x4mm, normal (0,1,0), area 14.5mm2, adj f0,f2,f7,f40,f42
  f40: plane 10x10mm, normal (0,0,-1), area 81.4mm2, adj f0,f2,f39,f41,f42,f47,f51,f52
  f41: plane 10x4mm, normal (0,-1,0), area 14.5mm2, adj f2,f7,f40,f42,f47
  f42: plane 10x1mm, normal (-1,0,0), area 10mm2, adj f7,f39,f40,f41
  f43: plane 10x4mm, normal (0,-1,0), area 14.5mm2, adj f2,f7,f45,f46,f48
  f44: plane 10x4mm, normal (0,1,0), area 14.5mm2, adj f1,f2,f7,f45,f46
  f45: plane 10x10mm, normal (0,0,-1), area 81.4mm2, adj f1,f2,f43,f44,f46,f48,f49,f50
  f46: plane 10x1mm, normal (-1,0,0), area 10mm2, adj f7,f43,f44,f45
  f47: plane 3x3mm, normal (-0.71,0,-0.71), area 4.2mm2, adj f2,f40,f41,f52
  f48: plane 3x3mm, normal (-0.71,0,-0.71), area 4.2mm2, adj f2,f43,f45,f50
  f49: plane 3x3mm, normal (0,-1,0), area 4.5mm2, adj f1,f2,f45
  f50: plane 3x3mm, normal (0,1,0), area 4.5mm2, adj f2,f45,f48
  f51: plane 3x3mm, normal (0,-1,0), area 4.5mm2, adj f0,f2,f40
  f52: plane 3x3mm, normal (0,1,0), area 4.5mm2, adj f2,f40,f47
  f53: cylinder r=2mm len=4mm, axis (0,0,1), area 12.6mm2, adj f7,f45
  f54: cylinder r=2mm len=4mm, axis (0,0,1), area 12.6mm2, adj f7,f40
PLACE A rot(axis=(1,0,0),0deg) t=(-217.65,-95.24,33.59)mm
PLACE B rot(axis=(1,0,0),90deg) t=(-39.92,-12.85,8.86)mm
PLACE C t=(-42.88,7.76,42.66)mm
PLACE D rot(axis=(0,0.71,-0.71),180deg) t=(43.62,-12.85,70.47)mm
PLACE E t=(-42.92,2.76,39.66)mm
MATE fastened D.f25 <-> C.f21  axis (0,-1,0) through (34.62,7.76,47.66)mm
MATE planar C.f24 <-> D.f41  axis (0,1,0) through (39.66,7.76,47.04)mm
MATE fastened D.f27 <-> A.f54  axis (0,1,0) through (-17.92,9.76,47.66)mm
MATE fastened E.f23 <-> D.f27  axis (0,1,0) through (-17.92,7.76,47.66)mm
MATE planar D.f41 <-> E.f18  axis (0,-1,0) through (8.35,7.76,48.64)mm
MATE fastened D.f103 <-> B.f81  axis (0,0,1) through (36.85,-6.85,39.66)mm
MATE planar B.f80 <-> D.f102  axis (0,0,-1) through (1.85,-17.89,39.66)mm
